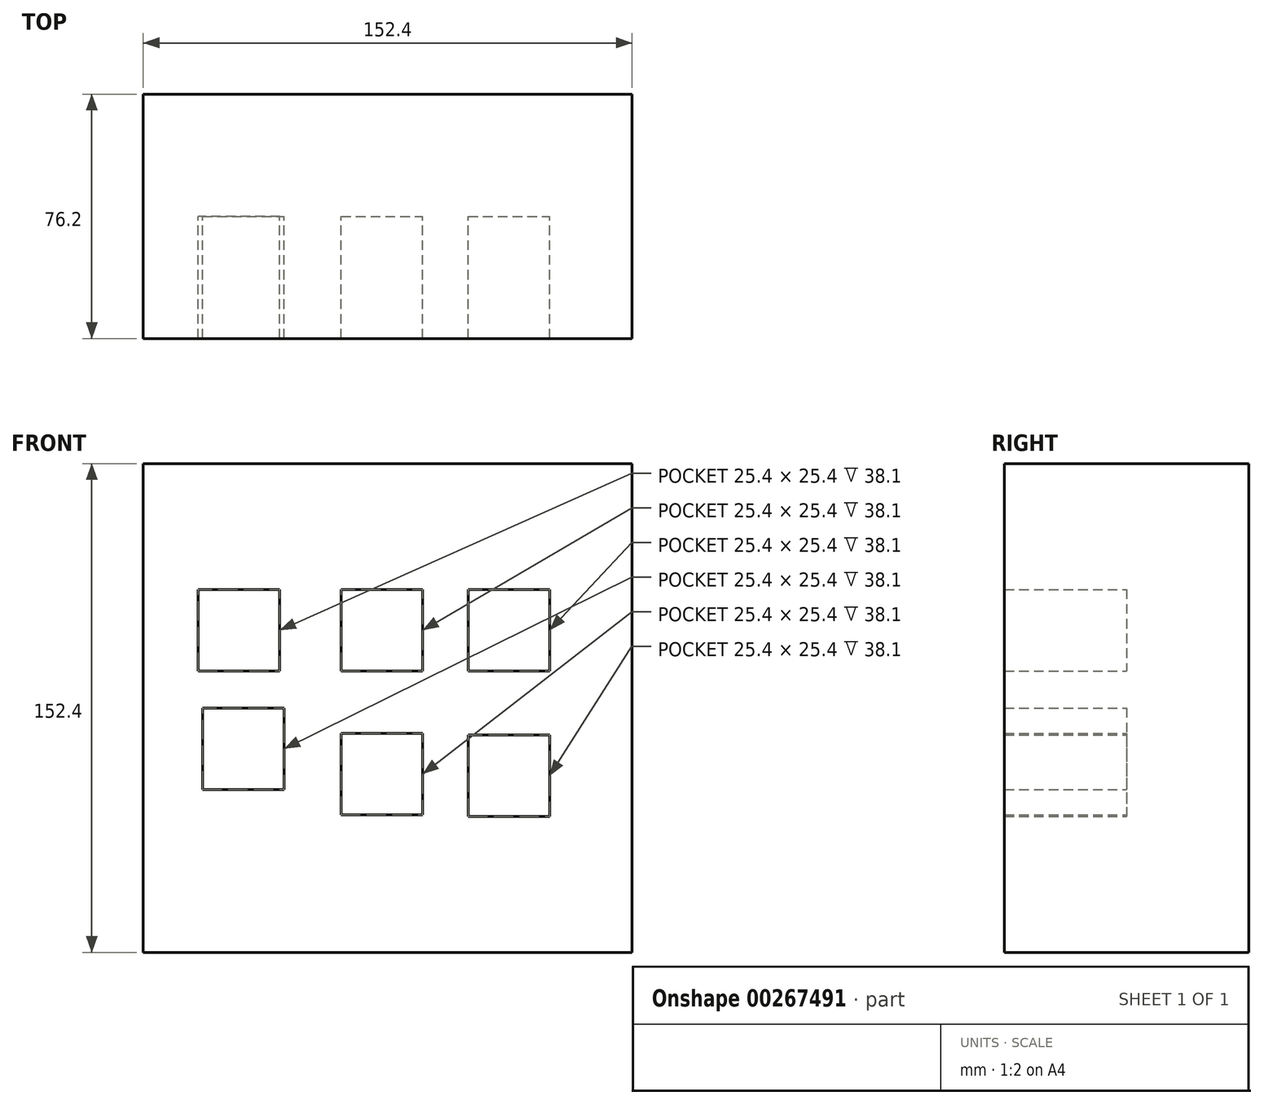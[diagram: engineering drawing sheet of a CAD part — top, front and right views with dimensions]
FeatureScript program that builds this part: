
annotation { "Feature Type Name" : "Feature", "Feature Type Description" : "" }
export const myFeature = defineFeature(function(context is Context, id is Id, definition is map)
    precondition{}
    {
        {
            var Q0;
            Q0=qCreatedBy(makeId("Front.planeOp"),FACE);
            var sketch = newSketch(context, id + "F0", { "sketchPlane" : qUnion([Q0])});
            skLineSegment(sketch, "E0.bottom", {"start": v(-76.2, 76.2) * mm, "end": v(76.2, 76.2) * mm});
            skLineSegment(sketch, "E0.top", {"start": v(-76.2, -76.2) * mm, "end": v(76.2, -76.2) * mm});
            skLineSegment(sketch, "E0.left", {"start": v(-76.2, 76.2) * mm, "end": v(-76.2, -76.2) * mm});
            skLineSegment(sketch, "E0.right", {"start": v(76.2, 76.2) * mm, "end": v(76.2, -76.2) * mm});
            skPoint(sketch, "E0.middle", {"position": v(0, 0) * mm});
            skLineSegment(sketch, "E1.bottom", {"start": v(-33.65, 36.97) * mm, "end": v(-59.05, 36.97) * mm});
            skLineSegment(sketch, "E1.top", {"start": v(-33.65, 11.57) * mm, "end": v(-59.05, 11.57) * mm});
            skLineSegment(sketch, "E1.left", {"start": v(-33.65, 36.97) * mm, "end": v(-33.65, 11.57) * mm});
            skLineSegment(sketch, "E1.right", {"start": v(-59.05, 36.97) * mm, "end": v(-59.05, 11.57) * mm});
            skPoint(sketch, "E1.middle", {"position": v(-46.35, 24.27) * mm});
            skLineSegment(sketch, "E2.bottom", {"start": v(-14.5, 36.97) * mm, "end": v(10.9, 36.97) * mm});
            skLineSegment(sketch, "E2.top", {"start": v(-14.5, 11.57) * mm, "end": v(10.9, 11.57) * mm});
            skLineSegment(sketch, "E2.left", {"start": v(-14.5, 36.97) * mm, "end": v(-14.5, 11.57) * mm});
            skLineSegment(sketch, "E2.right", {"start": v(10.9, 36.97) * mm, "end": v(10.9, 11.57) * mm});
            skPoint(sketch, "E2.middle", {"position": v(-1.8, 24.27) * mm});
            skLineSegment(sketch, "E3.bottom", {"start": v(25.15, 36.97) * mm, "end": v(50.55, 36.97) * mm});
            skLineSegment(sketch, "E3.top", {"start": v(25.15, 11.57) * mm, "end": v(50.55, 11.57) * mm});
            skLineSegment(sketch, "E3.left", {"start": v(25.15, 36.97) * mm, "end": v(25.15, 11.57) * mm});
            skLineSegment(sketch, "E3.right", {"start": v(50.55, 36.97) * mm, "end": v(50.55, 11.57) * mm});
            skPoint(sketch, "E3.middle", {"position": v(37.85, 24.27) * mm});
            skLineSegment(sketch, "E4.bottom", {"start": v(-57.69, 0) * mm, "end": v(-32.29, 0) * mm});
            skLineSegment(sketch, "E4.top", {"start": v(-57.69, -25.4) * mm, "end": v(-32.29, -25.4) * mm});
            skLineSegment(sketch, "E4.left", {"start": v(-57.69, 0) * mm, "end": v(-57.69, -25.4) * mm});
            skLineSegment(sketch, "E4.right", {"start": v(-32.29, 0) * mm, "end": v(-32.29, -25.4) * mm});
            skPoint(sketch, "E4.middle", {"position": v(-44.99, -12.7) * mm});
            skLineSegment(sketch, "E5.bottom", {"start": v(-14.5, -7.94) * mm, "end": v(10.9, -7.94) * mm});
            skLineSegment(sketch, "E5.top", {"start": v(-14.5, -33.34) * mm, "end": v(10.9, -33.34) * mm});
            skLineSegment(sketch, "E5.left", {"start": v(-14.5, -7.94) * mm, "end": v(-14.5, -33.34) * mm});
            skLineSegment(sketch, "E5.right", {"start": v(10.9, -7.94) * mm, "end": v(10.9, -33.34) * mm});
            skPoint(sketch, "E5.middle", {"position": v(-1.8, -20.64) * mm});
            skLineSegment(sketch, "E6.bottom", {"start": v(25.15, -8.49) * mm, "end": v(50.55, -8.49) * mm});
            skLineSegment(sketch, "E6.top", {"start": v(25.15, -33.89) * mm, "end": v(50.55, -33.89) * mm});
            skLineSegment(sketch, "E6.left", {"start": v(25.15, -8.49) * mm, "end": v(25.15, -33.89) * mm});
            skLineSegment(sketch, "E6.right", {"start": v(50.55, -8.49) * mm, "end": v(50.55, -33.89) * mm});
            skPoint(sketch, "E6.middle", {"position": v(37.85, -21.19) * mm});
            skSolve(sketch);
        }
        {
            var Q0;
            Q0=makeQuery(id+"F0.imprint","IMPRINT",FACE,{"disambiguationData":[TD([[makeQuery(id+"F0.imprint","IMPRINT",EDGE,{"derivedFrom":sQuery(id+"F0.wireOp",EDGE,"E0.bottom")}),-1.0]])]});
            extrude(context, id + "F1", {"entities" : qUnion([Q0]), "depth" : 76.2 * mm});
        }
        {
            var Q0;
            Q0=makeQuery(id+"F0.imprint","IMPRINT",FACE,{"disambiguationData":[TD([[makeQuery(id+"F0.imprint","IMPRINT",EDGE,{"derivedFrom":sQuery(id+"F0.wireOp",EDGE,"E1.bottom")}),1.0]])]});
            var Q1;
            Q1=makeQuery(id+"F0.imprint","IMPRINT",FACE,{"disambiguationData":[TD([[makeQuery(id+"F0.imprint","IMPRINT",EDGE,{"derivedFrom":sQuery(id+"F0.wireOp",EDGE,"E2.bottom")}),-1.0]])]});
            var Q2;
            Q2=makeQuery(id+"F0.imprint","IMPRINT",FACE,{"disambiguationData":[TD([[makeQuery(id+"F0.imprint","IMPRINT",EDGE,{"derivedFrom":sQuery(id+"F0.wireOp",EDGE,"E3.bottom")}),-1.0]])]});
            var Q3;
            Q3=makeQuery(id+"F0.imprint","IMPRINT",FACE,{"disambiguationData":[TD([[makeQuery(id+"F0.imprint","IMPRINT",EDGE,{"derivedFrom":sQuery(id+"F0.wireOp",EDGE,"E5.bottom")}),-1.0]])]});
            var Q4;
            Q4=makeQuery(id+"F0.imprint","IMPRINT",FACE,{"disambiguationData":[TD([[makeQuery(id+"F0.imprint","IMPRINT",EDGE,{"derivedFrom":sQuery(id+"F0.wireOp",EDGE,"E4.bottom")}),-1.0]])]});
            var Q5;
            Q5=makeQuery(id+"F0.imprint","IMPRINT",FACE,{"disambiguationData":[TD([[makeQuery(id+"F0.imprint","IMPRINT",EDGE,{"derivedFrom":sQuery(id+"F0.wireOp",EDGE,"E6.bottom")}),-1.0]])]});
            extrude(context, id + "F2", {"entities" : qUnion([Q0, Q1, Q2, Q3, Q4, Q5]), "operationType" : NewBodyOperationType.ADD, "depth" : 38.1 * mm});
        }
    });
